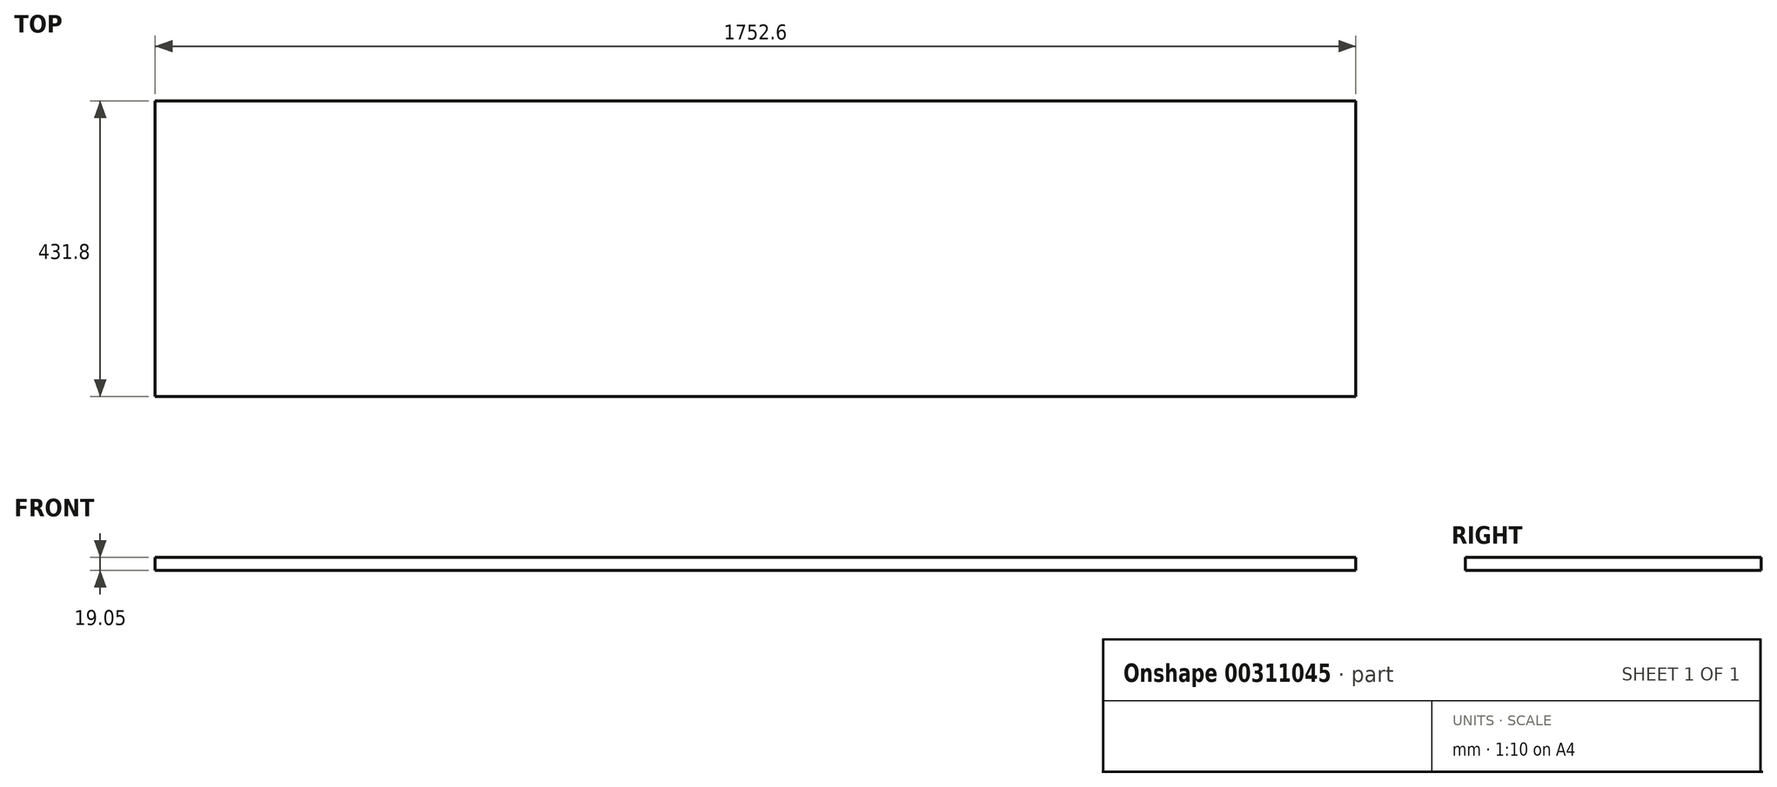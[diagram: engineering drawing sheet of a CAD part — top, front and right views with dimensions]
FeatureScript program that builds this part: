
annotation { "Feature Type Name" : "Feature", "Feature Type Description" : "" }
export const myFeature = defineFeature(function(context is Context, id is Id, definition is map)
    precondition{}
    {
        {
            var Q0;
            Q0=qCreatedBy(makeId("Top.planeOp"),FACE);
            var sketch = newSketch(context, id + "F0", { "sketchPlane" : qUnion([Q0])});
            skLineSegment(sketch, "E0.bottom", {"start": v(-885.42, 300.25) * mm, "end": v(867.18, 300.25) * mm});
            skLineSegment(sketch, "E0.top", {"start": v(-885.42, -131.55) * mm, "end": v(867.18, -131.55) * mm});
            skLineSegment(sketch, "E0.left", {"start": v(-885.42, 300.25) * mm, "end": v(-885.42, -131.55) * mm});
            skLineSegment(sketch, "E0.right", {"start": v(867.18, 300.25) * mm, "end": v(867.18, -131.55) * mm});
            skSolve(sketch);
        }
        {
            var Q0;
            Q0=makeQuery(id+"F0.imprint","IMPRINT",FACE,{"disambiguationData":[TD([[makeQuery(id+"F0.imprint","IMPRINT",EDGE,{"derivedFrom":sQuery(id+"F0.wireOp",EDGE,"E0.bottom")}),-1.0]])]});
            extrude(context, id + "F1", {"entities" : qUnion([Q0]), "depth" : 19.05 * mm});
        }
    });
